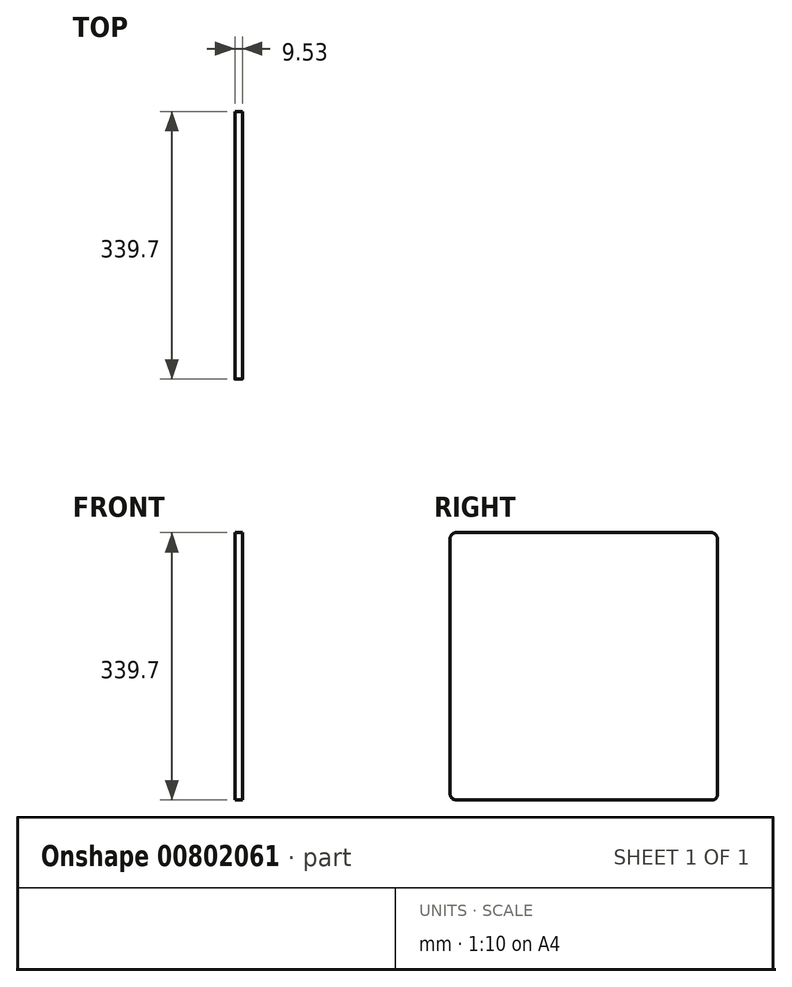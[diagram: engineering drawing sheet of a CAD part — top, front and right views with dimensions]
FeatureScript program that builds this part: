
annotation { "Feature Type Name" : "Feature", "Feature Type Description" : "" }
export const myFeature = defineFeature(function(context is Context, id is Id, definition is map)
    precondition{}
    {
        {
            var Q0;
            Q0=qCreatedBy(makeId("Right.planeOp"),FACE);
            var sketch = newSketch(context, id + "F0", { "sketchPlane" : qUnion([Q0])});
            skLineSegment(sketch, "E0.bottom", {"start": v(7.95, 0) * mm, "end": v(333.35, 0) * mm});
            skLineSegment(sketch, "E0.top", {"start": v(7.95, 339.7) * mm, "end": v(331.75, 339.7) * mm});
            skLineSegment(sketch, "E0.left", {"start": v(0, 7.95) * mm, "end": v(0, 331.75) * mm});
            skLineSegment(sketch, "E0.right", {"start": v(339.7, 6.35) * mm, "end": v(339.7, 331.75) * mm});
            skPoint(sketch, "E1.visualSharp", {"position": v(339.7, 339.7) * mm});
            skArc(sketch, "E1.filletArc", {"start": v(339.7, 331.75) * mm, "mid": v(337.37, 337.37) * mm, "end": v(331.75, 339.7) * mm});
            skPoint(sketch, "E2.visualSharp", {"position": v(339.7, 0) * mm});
            skPoint(sketch, "E3.visualSharp", {"position": v(0, 0) * mm});
            skArc(sketch, "E3.filletArc", {"start": v(0, 7.95) * mm, "mid": v(2.33, 2.33) * mm, "end": v(7.95, 0) * mm});
            skPoint(sketch, "E4.orphan", {"position": v(0, 339.7) * mm});
            skPoint(sketch, "E5.visualSharp", {"position": v(242.85, 96.85) * mm});
            skArc(sketch, "E6.filletArc", {"start": v(333.35, 0) * mm, "mid": v(337.84, 1.86) * mm, "end": v(339.7, 6.35) * mm});
            skArc(sketch, "E7.filletArc", {"start": v(7.95, 339.7) * mm, "mid": v(2.33, 337.37) * mm, "end": v(0, 331.75) * mm});
            skSolve(sketch);
        }
        {
            var Q0;
            Q0=qSketchRegion(id+"F0",true);
            extrude(context, id + "F1", {"entities" : qUnion([Q0]), "depth" : 9.53 * mm});
        }
    });
